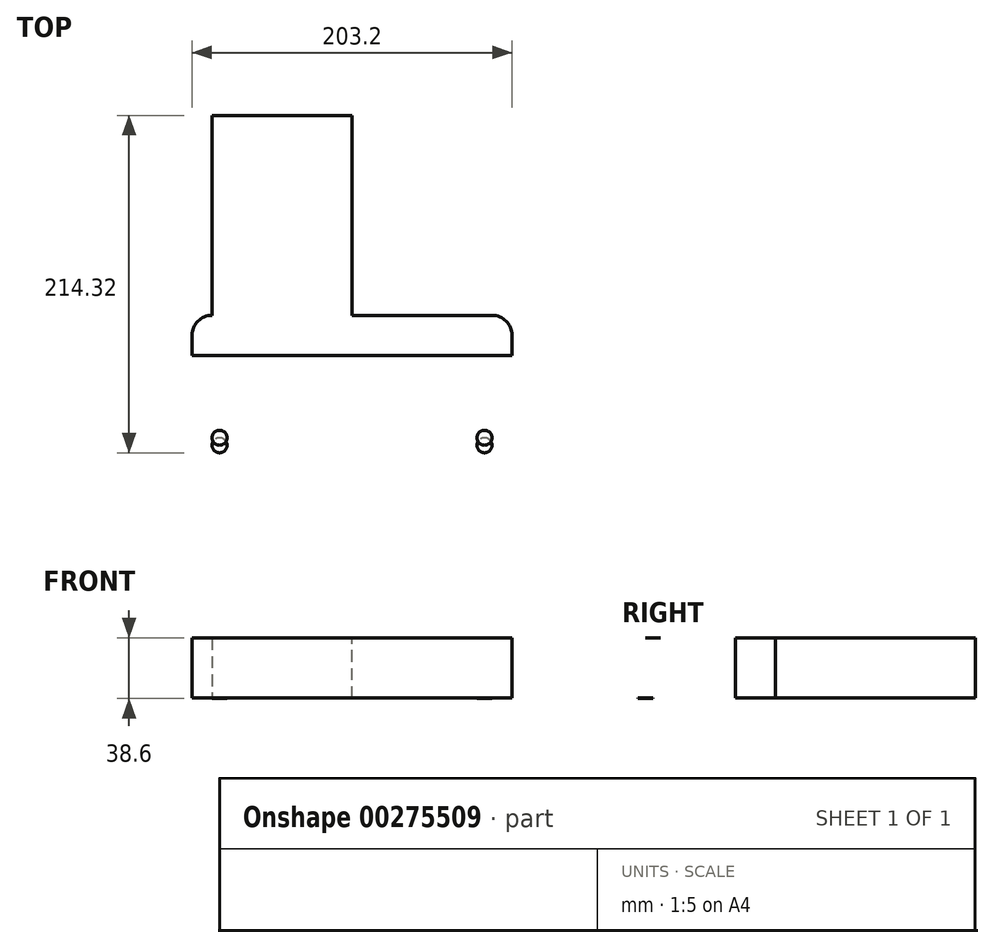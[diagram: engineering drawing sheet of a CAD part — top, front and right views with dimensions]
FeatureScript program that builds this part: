
annotation { "Feature Type Name" : "Feature", "Feature Type Description" : "" }
export const myFeature = defineFeature(function(context is Context, id is Id, definition is map)
    precondition{}
    {
        {
            var Q0;
            Q0=qCreatedBy(makeId("Top.planeOp"),FACE);
            var sketch = newSketch(context, id + "F0", { "sketchPlane" : qUnion([Q0])});
            skLineSegment(sketch, "E0.bottom", {"start": v(-80.27, 58.74) * mm, "end": v(97.53, 58.74) * mm});
            skLineSegment(sketch, "E0.top", {"start": v(-92.97, 33.34) * mm, "end": v(110.23, 33.34) * mm});
            skLineSegment(sketch, "E0.left", {"start": v(-92.97, 46.04) * mm, "end": v(-92.97, 33.34) * mm});
            skLineSegment(sketch, "E0.right", {"start": v(110.23, 46.04) * mm, "end": v(110.23, 33.34) * mm});
            skLineSegment(sketch, "E1.bottom", {"start": v(-92.97, 33.34) * mm, "end": v(-57.4, 33.34) * mm});
            skLineSegment(sketch, "E1.top", {"start": v(-92.97, -42.86) * mm, "end": v(-57.4, -42.86) * mm});
            skLineSegment(sketch, "E1.left", {"start": v(-92.97, 33.34) * mm, "end": v(-92.97, -42.86) * mm});
            skLineSegment(sketch, "E1.right", {"start": v(-57.4, 33.34) * mm, "end": v(-57.4, -42.86) * mm});
            skLineSegment(sketch, "E2.bottom", {"start": v(110.23, 33.34) * mm, "end": v(74.67, 33.34) * mm});
            skLineSegment(sketch, "E2.top", {"start": v(110.23, -42.86) * mm, "end": v(74.67, -42.86) * mm});
            skLineSegment(sketch, "E2.left", {"start": v(110.23, 33.34) * mm, "end": v(110.23, -42.86) * mm});
            skLineSegment(sketch, "E2.right", {"start": v(74.67, 33.34) * mm, "end": v(74.67, -42.86) * mm});
            skPoint(sketch, "E3.visualSharp", {"position": v(-92.97, 58.74) * mm});
            skArc(sketch, "E3.filletArc", {"start": v(-80.27, 58.74) * mm, "mid": v(-89.25, 55.02) * mm, "end": v(-92.97, 46.04) * mm});
            skPoint(sketch, "E4.visualSharp", {"position": v(110.23, 58.74) * mm});
            skArc(sketch, "E4.filletArc", {"start": v(110.23, 46.04) * mm, "mid": v(106.51, 55.02) * mm, "end": v(97.53, 58.74) * mm});
            skSolve(sketch);
        }
        {
            var Q0;
            Q0=makeQuery(id+"F0.imprint","IMPRINT",FACE,{"disambiguationData":[TD([[makeQuery(id+"F0.imprint","IMPRINT",EDGE,{"derivedFrom":sQuery(id+"F0.wireOp",EDGE,"E0.bottom")}),-1.0]])]});
            var Q1;
            Q1=makeQuery(id+"F0.imprint","IMPRINT",FACE,{"disambiguationData":[TD([[makeQuery(id+"F0.imprint","IMPRINT",EDGE,{"derivedFrom":sQuery(id+"F0.wireOp",EDGE,"E1.bottom")}),-1.0]])]});
            var Q2;
            Q2=makeQuery(id+"F0.imprint","IMPRINT",FACE,{"disambiguationData":[TD([[makeQuery(id+"F0.imprint","IMPRINT",EDGE,{"derivedFrom":sQuery(id+"F0.wireOp",EDGE,"E2.bottom")}),1.0]])]});
            extrude(context, id + "F1", {"entities" : qUnion([Q0, Q1, Q2]), "depth" : 38.1 * mm});
        }
        {
            var Q0;
            Q0=makeQuery(id+"F1.opExtrude","CAP_FACE",FACE,{"disambiguationData":[OSD([sQuery(id+"F0.wireOp",EDGE,"E0.bottom"),sQuery(id+"F0.wireOp",EDGE,"E0.top"),sQuery(id+"F0.wireOp",EDGE,"E0.left"),sQuery(id+"F0.wireOp",EDGE,"E0.right"),sQuery(id+"F0.wireOp",EDGE,"E1.top"),sQuery(id+"F0.wireOp",EDGE,"E1.left"),sQuery(id+"F0.wireOp",EDGE,"E1.right"),sQuery(id+"F0.wireOp",EDGE,"E2.top"),sQuery(id+"F0.wireOp",EDGE,"E2.left"),sQuery(id+"F0.wireOp",EDGE,"E2.right"),sQuery(id+"F0.wireOp",EDGE,"E3.filletArc"),sQuery(id+"F0.wireOp",EDGE,"E4.filletArc")])],"isStart":false});
            var sketch = newSketch(context, id + "F2", { "sketchPlane" : qUnion([Q0])});
            skCircle(sketch, "E5", {"center": v(-75.5, -19.05) * mm, "radius": 4.76 * mm});
            skCircle(sketch, "E6", {"center": v(92.77, -19.05) * mm, "radius": 4.76 * mm});
            skSolve(sketch);
        }
        {
            var Q0;
            Q0 = qSketchRegion(id + "F2", true);
            extrude(context, id + "F3", {"entities" : qUnion([Q0]), "operationType" : NewBodyOperationType.ADD, "depth" : 0.25 * mm});
        }
        {
            var Q0;
            Q0=makeQuery(id+"F1.opExtrude","SWEPT_FACE",FACE,{"disambiguationData":[OSD([sQuery(id+"F0.wireOp",EDGE,"E0.bottom")])]});
            var sketch = newSketch(context, id + "F4", { "sketchPlane" : qUnion([Q0])});
            skLineSegment(sketch, "E7", {"start": v(-97.53, 19.05) * mm, "end": v(80.27, 19.05) * mm});
            skLineSegment(sketch, "E8", {"start": v(-8.63, 19.05) * mm, "end": v(-8.63, 38.1) * mm});
            skLineSegment(sketch, "E9", {"start": v(-8.63, 38.1) * mm, "end": v(-8.63, 0) * mm});
            skCircle(sketch, "E10", {"center": v(-8.63, 19.05) * mm, "radius": 11.11 * mm});
            skSolve(sketch);
        }
        {
            var Q0;
            {var subQ0=sQuery(id+"F4.wireOp",EDGE,"E10");var subQ1=sQuery(id+"F4.wireOp",EDGE,"E7");var subQ2=makeQuery(id+"F4.imprint","INTERSECT",VERTEX,{"disambiguationData":[OD(0.0)],"derivedFrom":[subQ1,subQ0]});Q0=makeQuery(id+"F4.imprint","IMPRINT",FACE,{"disambiguationData":[TD([[makeQuery(id+"F4.imprint","IMPRINT",EDGE,{"disambiguationData":[TD([[subQ2,-1.0]])],"derivedFrom":subQ1}),1.0]])]});}
            var Q1;
            {var subQ0=sQuery(id+"F4.wireOp",EDGE,"E9");var subQ1=sQuery(id+"F4.wireOp",EDGE,"E7");var subQ2=makeQuery(id+"F4.imprint","INTERSECT",VERTEX,{"derivedFrom":[subQ1,subQ0]});Q1=makeQuery(id+"F4.imprint","IMPRINT",FACE,{"disambiguationData":[TD([[makeQuery(id+"F4.imprint","IMPRINT",EDGE,{"disambiguationData":[TD([[subQ2,-1.0]])],"derivedFrom":subQ1}),1.0]])]});}
            var Q2;
            {var subQ0=sQuery(id+"F4.wireOp",EDGE,"E9");var subQ1=sQuery(id+"F4.wireOp",EDGE,"E7");var subQ2=makeQuery(id+"F4.imprint","INTERSECT",VERTEX,{"derivedFrom":[subQ1,subQ0]});Q2=makeQuery(id+"F4.imprint","IMPRINT",FACE,{"disambiguationData":[TD([[makeQuery(id+"F4.imprint","IMPRINT",EDGE,{"disambiguationData":[TD([[subQ2,-1.0]])],"derivedFrom":subQ1}),-1.0]])]});}
            var Q3;
            {var subQ0=sQuery(id+"F4.wireOp",EDGE,"E10");var subQ1=sQuery(id+"F4.wireOp",EDGE,"E7");var subQ2=makeQuery(id+"F4.imprint","INTERSECT",VERTEX,{"disambiguationData":[OD(0.0)],"derivedFrom":[subQ1,subQ0]});Q3=makeQuery(id+"F4.imprint","IMPRINT",FACE,{"disambiguationData":[TD([[makeQuery(id+"F4.imprint","IMPRINT",EDGE,{"disambiguationData":[TD([[subQ2,-1.0]])],"derivedFrom":subQ1}),-1.0]])]});}
            extrude(context, id + "F5", {"entities" : qUnion([Q0, Q1, Q2, Q3]), "operationType" : NewBodyOperationType.ADD, "depth" : 127 * mm});
        }
        {
            var Q0;
            Q0=makeQuery(id+"F1.opExtrude","CAP_FACE",FACE,{"disambiguationData":[OSD([sQuery(id+"F0.wireOp",EDGE,"E0.bottom"),sQuery(id+"F0.wireOp",EDGE,"E0.top"),sQuery(id+"F0.wireOp",EDGE,"E0.left"),sQuery(id+"F0.wireOp",EDGE,"E0.right"),sQuery(id+"F0.wireOp",EDGE,"E1.top"),sQuery(id+"F0.wireOp",EDGE,"E1.left"),sQuery(id+"F0.wireOp",EDGE,"E1.right"),sQuery(id+"F0.wireOp",EDGE,"E2.top"),sQuery(id+"F0.wireOp",EDGE,"E2.left"),sQuery(id+"F0.wireOp",EDGE,"E2.right"),sQuery(id+"F0.wireOp",EDGE,"E3.filletArc"),sQuery(id+"F0.wireOp",EDGE,"E4.filletArc")])],"isStart":true});
            var sketch = newSketch(context, id + "F6", { "sketchPlane" : qUnion([Q0])});
            skCircle(sketch, "E11", {"center": v(-75.5, 23.81) * mm, "radius": 4.76 * mm});
            skCircle(sketch, "E12", {"center": v(92.77, 23.81) * mm, "radius": 4.76 * mm});
            skSolve(sketch);
        }
        {
            var Q0;
            Q0=makeQuery(id+"F6.imprint","IMPRINT",FACE,{"disambiguationData":[TD([[makeQuery(id+"F6.imprint","IMPRINT",EDGE,{"derivedFrom":sQuery(id+"F6.wireOp",EDGE,"E11")}),1.0]])]});
            var Q1;
            Q1=makeQuery(id+"F6.imprint","IMPRINT",FACE,{"disambiguationData":[TD([[makeQuery(id+"F6.imprint","IMPRINT",EDGE,{"derivedFrom":sQuery(id+"F6.wireOp",EDGE,"E12")}),1.0]])]});
            extrude(context, id + "F7", {"entities" : qUnion([Q0, Q1]), "operationType" : NewBodyOperationType.ADD, "depth" : 0.25 * mm});
        }
    });
